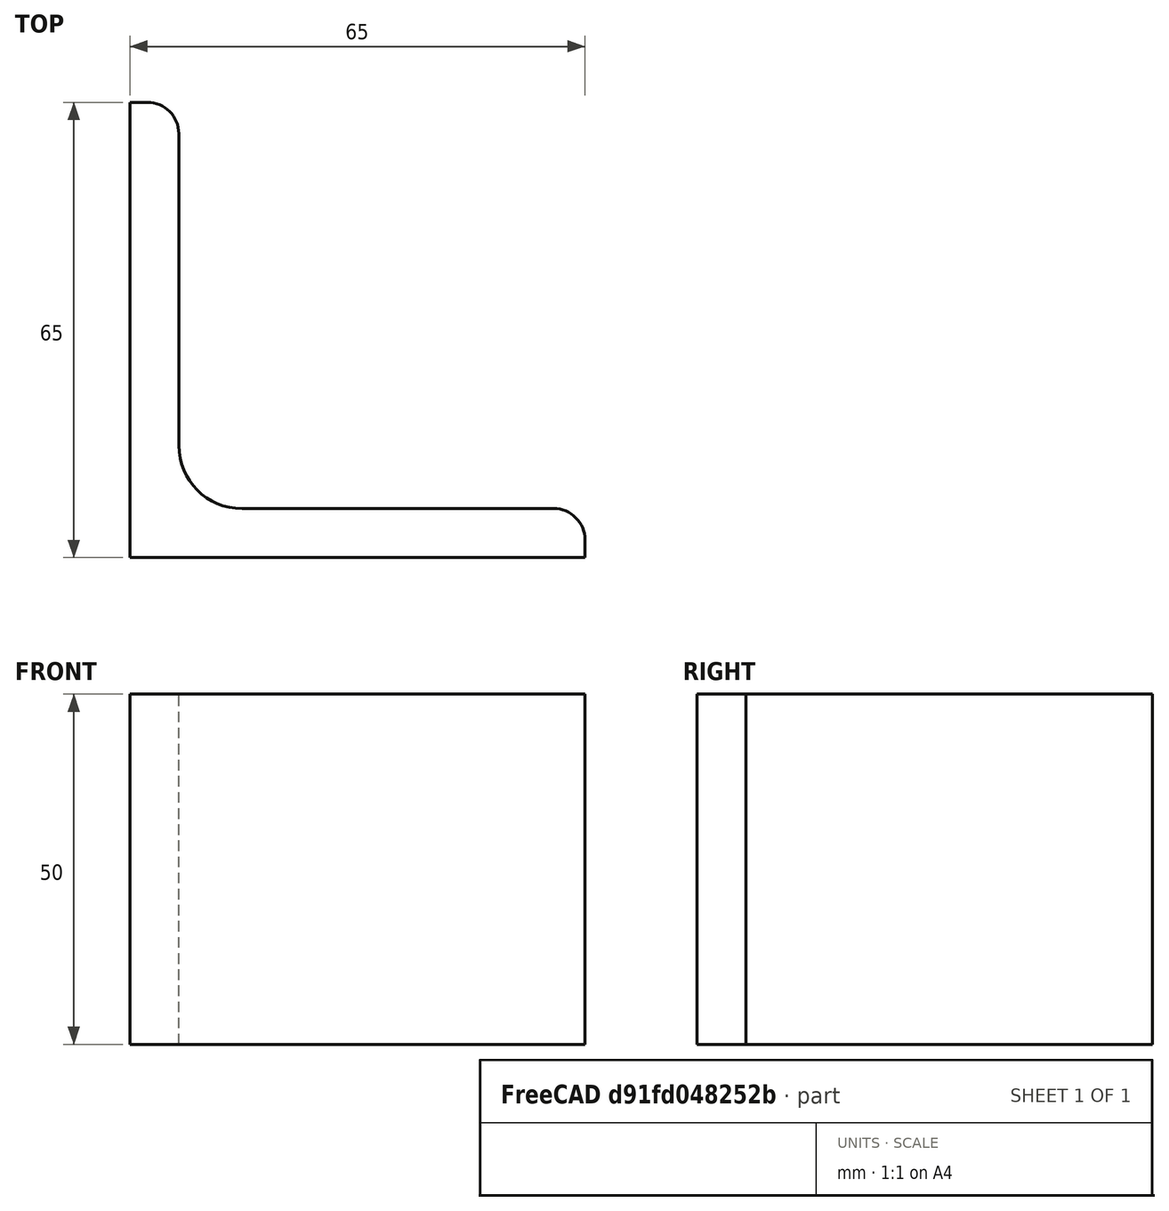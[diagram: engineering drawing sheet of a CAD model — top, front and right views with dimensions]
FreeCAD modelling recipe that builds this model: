
FCSTD DOCUMENT  (FreeCAD 0.15R4671 (Git))
Label: Angle Bar L65x65x7 EN10056 S235JR
License: All rights reserved
LicenseURL: http://en.wikipedia.org/wiki/All_rights_reserved
objects: Sketcher::SketchObject×1, Part::Extrusion×1
note: 2 computed .brp shape members not serialized (recipe doc carries the construction recipe); baked Part::Feature solids carry a one-line shape summary decoded from their .brp

FEATURE [Sketcher::SketchObject] Sketch
  sketch-geometry (9):
    g0: LineSegment StartX=0 StartY=0 StartZ=0 EndX=65 EndY=0 EndZ=0
    g1: LineSegment StartX=65 StartY=0 StartZ=0 EndX=65 EndY=2.5 EndZ=0
    g2: LineSegment StartX=60.5 StartY=7 StartZ=0 EndX=16 EndY=7 EndZ=0
    g3: LineSegment StartX=0 StartY=0 StartZ=0 EndX=0 EndY=65 EndZ=0
    g4: LineSegment StartX=0 StartY=65 StartZ=0 EndX=2.5 EndY=65 EndZ=0
    g5: LineSegment StartX=7 StartY=60.5 StartZ=0 EndX=7 EndY=16 EndZ=0
    g6: ArcOfCircle CenterX=16 CenterY=16 CenterZ=0 NormalX=0 NormalY=0 NormalZ=1 Radius=9 StartAngle=3.14159 EndAngle=4.71239
    g7: ArcOfCircle CenterX=2.5 CenterY=60.5 CenterZ=0 NormalX=0 NormalY=0 NormalZ=1 Radius=4.5 StartAngle=0 EndAngle=1.5708
    g8: ArcOfCircle CenterX=60.5 CenterY=2.5 CenterZ=0 NormalX=0 NormalY=0 NormalZ=1 Radius=4.5 StartAngle=0 EndAngle=1.5708
  constraints (23):
    c: Coincident(g0,g-1)
    c: Horizontal(g0)
    c: Coincident(g1,g0)
    c: Vertical(g1)
    c: Horizontal(g2)
    c: Coincident(g3,g-1)
    c: Vertical(g3)
    c: Coincident(g4,g3)
    c: Horizontal(g4)
    c: Vertical(g5)
    c: Tangent(g5,g6) = -1.5708
    c: Tangent(g2,g6) = 1.5708
    c: Tangent(g4,g7) = 1.5708
    c: Tangent(g5,g7) = 1.5708
    c: Tangent(g2,g8) = -1.5708
    c: Tangent(g1,g8) = -1.5708
    c: DistanceX(g0) = 65
    c: DistanceY(g3) = 65
    c: DistanceY(g0,g2) = 7
    c: DistanceX(g3,g5) = 7
    c: Radius(g6) = 9
    c: Radius(g8) = 4.5
    c: Radius(g7) = 4.5
FEATURE [Part::Extrusion] Extrude  label="Angle Bar L65x65x7 EN10056 S235JR"
  Base = -> Sketch
  Dir = (0,0,50)
  Solid = true
